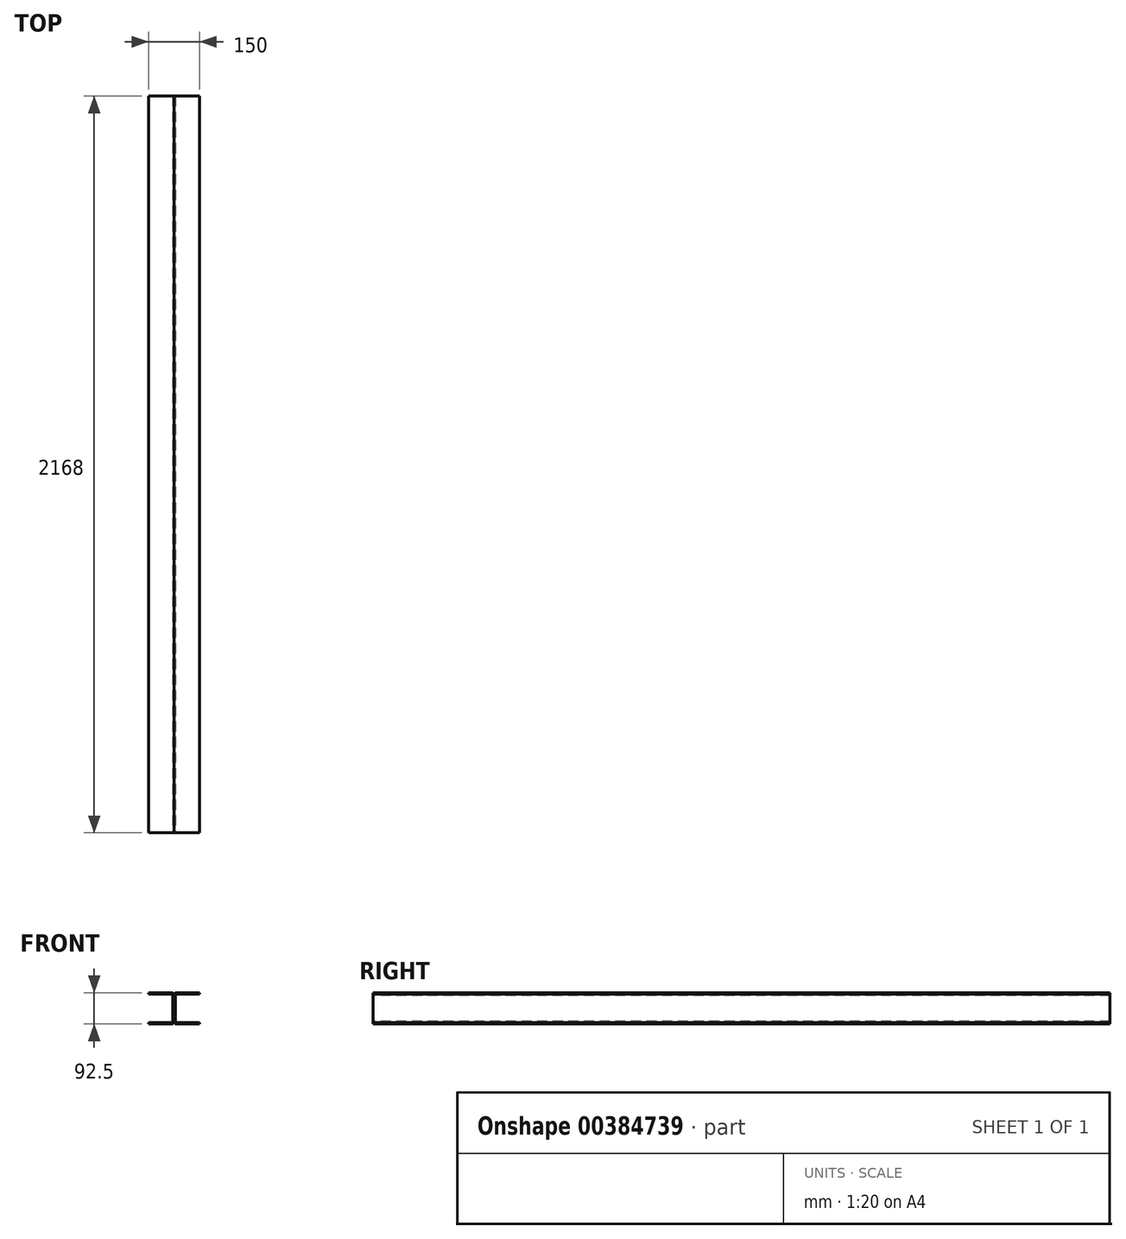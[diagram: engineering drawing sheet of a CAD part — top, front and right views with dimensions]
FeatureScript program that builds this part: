
annotation { "Feature Type Name" : "Feature", "Feature Type Description" : "" }
export const myFeature = defineFeature(function(context is Context, id is Id, definition is map)
    precondition{}
    {
        {
            var Q0;
            Q0=qCreatedBy(makeId("Front.planeOp"),FACE);
            var sketch = newSketch(context, id + "F0", { "sketchPlane" : qUnion([Q0])});
            skLineSegment(sketch, "E0.bottom", {"start": v(-75, -46.25) * mm, "end": v(-8, -46.25) * mm});
            skLineSegment(sketch, "E0.top", {"start": v(-75, 46.25) * mm, "end": v(-8, 46.25) * mm});
            skLineSegment(sketch, "E0.left", {"start": v(-75, -46.25) * mm, "end": v(-75, -42.25) * mm});
            skLineSegment(sketch, "E0.right", {"start": v(75, -46.25) * mm, "end": v(75, -42.25) * mm});
            skPoint(sketch, "E0.middle", {"position": v(0, 0) * mm});
            skLineSegment(sketch, "E1.bottom", {"start": v(-75, -42.25) * mm, "end": v(-8, -42.25) * mm});
            skLineSegment(sketch, "E1.top", {"start": v(-75, 42.25) * mm, "end": v(-8, 42.25) * mm});
            skLineSegment(sketch, "E1.right", {"start": v(-4, -38.25) * mm, "end": v(-4, 38.25) * mm});
            skPoint(sketch, "E1.middle", {"position": v(-37.5, 0) * mm});
            skLineSegment(sketch, "E2.bottom", {"start": v(8, -42.25) * mm, "end": v(75, -42.25) * mm});
            skLineSegment(sketch, "E2.top", {"start": v(8, 42.25) * mm, "end": v(75, 42.25) * mm});
            skLineSegment(sketch, "E2.left", {"start": v(4, -38.25) * mm, "end": v(4, 38.25) * mm});
            skPoint(sketch, "E2.middle", {"position": v(37.5, 0) * mm});
            skPoint(sketch, "E1.left.end.orphan", {"position": v(-71, 42.25) * mm});
            skPoint(sketch, "E1.left.start.orphan", {"position": v(-71, -42.25) * mm});
            skLineSegment(sketch, "E3.trimOffspring", {"start": v(-75, 42.25) * mm, "end": v(-75, 46.25) * mm});
            skPoint(sketch, "E2.right.end.orphan", {"position": v(71, 42.25) * mm});
            skPoint(sketch, "E2.right.start.orphan", {"position": v(71, -42.25) * mm});
            skLineSegment(sketch, "E4.trimOffspring", {"start": v(75, 42.25) * mm, "end": v(75, 46.25) * mm});
            skLineSegment(sketch, "E5", {"start": v(0, -38.25) * mm, "end": v(0, 38.25) * mm});
            skPoint(sketch, "E6.visualSharp", {"position": v(-4, 42.25) * mm});
            skArc(sketch, "E6.filletArc", {"start": v(-4, 38.25) * mm, "mid": v(-5.17, 41.08) * mm, "end": v(-8, 42.25) * mm});
            skPoint(sketch, "E7.visualSharp", {"position": v(4, 42.25) * mm});
            skArc(sketch, "E7.filletArc", {"start": v(8, 42.25) * mm, "mid": v(5.17, 41.08) * mm, "end": v(4, 38.25) * mm});
            skPoint(sketch, "E8.visualSharp", {"position": v(4, -42.25) * mm});
            skArc(sketch, "E8.filletArc", {"start": v(4, -38.25) * mm, "mid": v(5.17, -41.08) * mm, "end": v(8, -42.25) * mm});
            skPoint(sketch, "E9.visualSharp", {"position": v(-4, -42.25) * mm});
            skArc(sketch, "E9.filletArc", {"start": v(-8, -42.25) * mm, "mid": v(-5.17, -41.08) * mm, "end": v(-4, -38.25) * mm});
            skPoint(sketch, "E10.newPointA", {"position": v(75, 46.25) * mm});
            skPoint(sketch, "E10.newPointB", {"position": v(0, 46.25) * mm});
            skArc(sketch, "E10.filletArc", {"start": v(0, 38.25) * mm, "mid": v(-2.34, 43.9) * mm, "end": v(-8, 46.25) * mm});
            skLineSegment(sketch, "E11", {"start": v(8, 46.25) * mm, "end": v(75, 46.25) * mm});
            skLineSegment(sketch, "E12", {"start": v(0, 38.25) * mm, "end": v(0, 38.25) * mm});
            skArc(sketch, "E13.filletArc", {"start": v(8, 46.25) * mm, "mid": v(2.34, 43.9) * mm, "end": v(0, 38.25) * mm});
            skPoint(sketch, "E14.newPointA", {"position": v(75, -46.25) * mm});
            skPoint(sketch, "E14.newPointB", {"position": v(0, -46.25) * mm});
            skArc(sketch, "E14.filletArc", {"start": v(-8, -46.25) * mm, "mid": v(-2.34, -43.9) * mm, "end": v(0, -38.25) * mm});
            skLineSegment(sketch, "E15", {"start": v(0, -38.25) * mm, "end": v(0, -38.25) * mm});
            skLineSegment(sketch, "E16", {"start": v(8, -46.25) * mm, "end": v(75, -46.25) * mm});
            skArc(sketch, "E17.filletArc", {"start": v(0, -38.25) * mm, "mid": v(2.34, -43.9) * mm, "end": v(8, -46.25) * mm});
            skSolve(sketch);
        }
        {
            var Q0;
            Q0=makeQuery(id+"F0.imprint","IMPRINT",FACE,{"disambiguationData":[TD([[makeQuery(id+"F0.imprint","IMPRINT",EDGE,{"derivedFrom":sQuery(id+"F0.wireOp",EDGE,"E0.right")}),1.0]])]});
            var Q1;
            Q1=makeQuery(id+"F0.imprint","IMPRINT",FACE,{"disambiguationData":[TD([[makeQuery(id+"F0.imprint","IMPRINT",EDGE,{"derivedFrom":sQuery(id+"F0.wireOp",EDGE,"E0.bottom")}),1.0]])]});
            extrude(context, id + "F1", {"entities" : qUnion([Q0, Q1]), "oppositeDirection" : true, "depth" : 2168 * mm});
        }
    });
